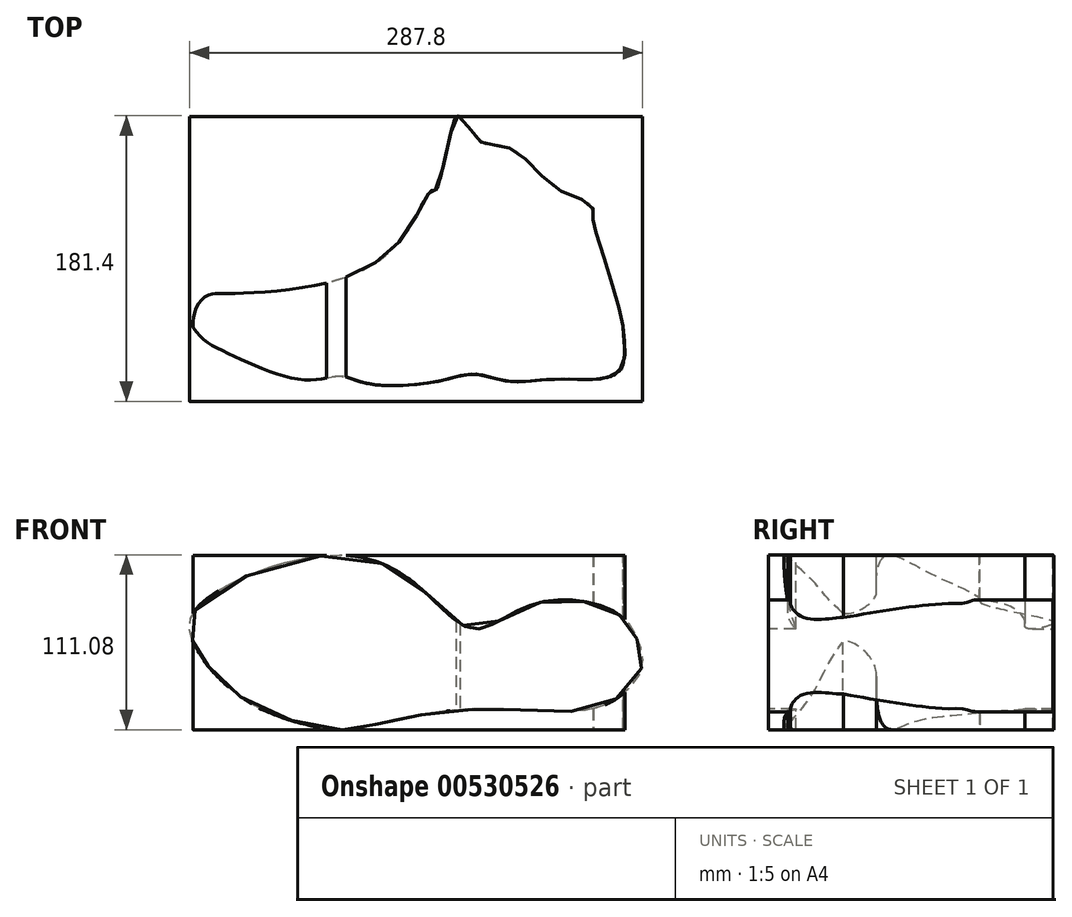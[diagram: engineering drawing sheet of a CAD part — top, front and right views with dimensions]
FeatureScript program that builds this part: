
annotation { "Feature Type Name" : "Feature", "Feature Type Description" : "" }
export const myFeature = defineFeature(function(context is Context, id is Id, definition is map)
    precondition{}
    {
        {
            var Q0;
            Q0=qCreatedBy(makeId("Top.planeOp"),FACE);
            var sketch = newSketch(context, id + "F0", { "sketchPlane" : qUnion([Q0])});
            skSolve(sketch);
        }
        {
            var Q0;
            Q0=qCreatedBy(makeId("Top.planeOp"),FACE);
            var sketch = newSketch(context, id + "F1", { "sketchPlane" : qUnion([Q0])});
            skFitSpline(sketch, "E0", {"points": [v(11, 46.88) * mm, v(33.23, 30.49) * mm, v(81.02, 13.66) * mm, v(104.72, 15.94) * mm, v(121.56, 11.33) * mm, v(166.6, 12.76) * mm, v(189.8, 17.31) * mm, v(210.72, 12.76) * mm, v(244.38, 14.13) * mm, v(283.14, 20.97) * mm, v(283.96, 47.8) * mm], "startDerivative": vector(161.26, -262) * mm, "endDerivative": vector(25.45, 106.25) * mm});
            skFitSpline(sketch, "E1", {"points": [v(11, 46.88) * mm, v(11, 52.93) * mm, v(16.15, 64.44) * mm, v(23.74, 68.45) * mm, v(30.78, 68.52) * mm, v(93.22, 74.7) * mm, v(144.77, 105.04) * mm, v(162.74, 134.2) * mm, v(165.1, 134.5) * mm, v(177.47, 179.85) * mm, v(180.41, 180.74) * mm, v(193.96, 164.54) * mm, v(204.27, 162.77) * mm, v(219.92, 155.97) * mm, v(243.66, 134.01) * mm, v(264.04, 124.52) * mm, v(265.03, 117.2) * mm, v(266.02, 110.08) * mm, v(278.1, 71.1) * mm, v(283.96, 47.8) * mm], "startDerivative": vector(-19.57, 179.88) * mm, "endDerivative": vector(74.73, -338.84) * mm});
            skSolve(sketch);
        }
        {
            var Q0;
            Q0=qCreatedBy(makeId("Front.planeOp"),FACE);
            var sketch = newSketch(context, id + "F2", { "sketchPlane" : qUnion([Q0])});
            skFitSpline(sketch, "E2", {"points": [v(10.6, 0) * mm, v(11.73, 18.85) * mm, v(95.63, 54.43) * mm, v(155.55, 33.46) * mm, v(189.26, 7.61) * mm, v(219.97, 20.72) * mm, v(258.17, 25.22) * mm, v(284.01, 14.73) * mm, v(293.38, 0) * mm, v(295.62, -17.48) * mm, v(272.4, -40.7) * mm, v(224.84, -44.07) * mm, v(177.65, -44.07) * mm, v(129.33, -52.31) * mm, v(106.49, -56.43) * mm, v(51.43, -41.83) * mm, v(19.22, -14.48) * mm, v(10.6, 0) * mm]});
            skSolve(sketch);
        }
        {
            var Q0;
            Q0=makeQuery(id+"F2.imprint","IMPRINT",FACE,{"disambiguationData":[TD([[makeQuery(id+"F2.imprint","IMPRINT",EDGE,{"derivedFrom":sQuery(id+"F2.wireOp",EDGE,"E2")}),-1.0]])]});
            var Q1;
            Q1=sQuery(id+"F2.wireOp",EDGE,"E2");
            var Q2;
            Q2=sQuery(id+"F1.wireOp",VERTEX,"E1.10.internal");
            extrude(context, id + "F3", {"entities" : qUnion([Q0]), "surfaceEntities" : qUnion([Q1]), "endBound" : BoundingType.UP_TO_VERTEX, "oppositeDirection" : true, "depth" : 25.4 * mm, "endBoundEntityVertex" : qUnion([Q2]), "offsetDistance" : 25.4 * mm});
        }
        {
            var Q0;
            Q0 = qSketchRegion(id + "F1", true);
            var Q1;
            Q1=sQuery(id+"F2.wireOp",VERTEX,"E2.2.internal");
            var Q2;
            Q2=sQuery(id+"F2.wireOp",VERTEX,"E2.14.internal");
            extrude(context, id + "F4", {"entities" : qUnion([Q0]), "operationType" : NewBodyOperationType.ADD, "endBound" : BoundingType.UP_TO_VERTEX, "depth" : 25.4 * mm, "endBoundEntityVertex" : qUnion([Q1]), "offsetDistance" : 25.4 * mm, "hasSecondDirection" : true, "secondDirectionBound" : BoundingType.UP_TO_VERTEX, "secondDirectionOppositeDirection" : true, "secondDirectionDepth" : 25.4 * mm, "secondDirectionBoundEntityVertex" : qUnion([Q2])});
        }
    });
